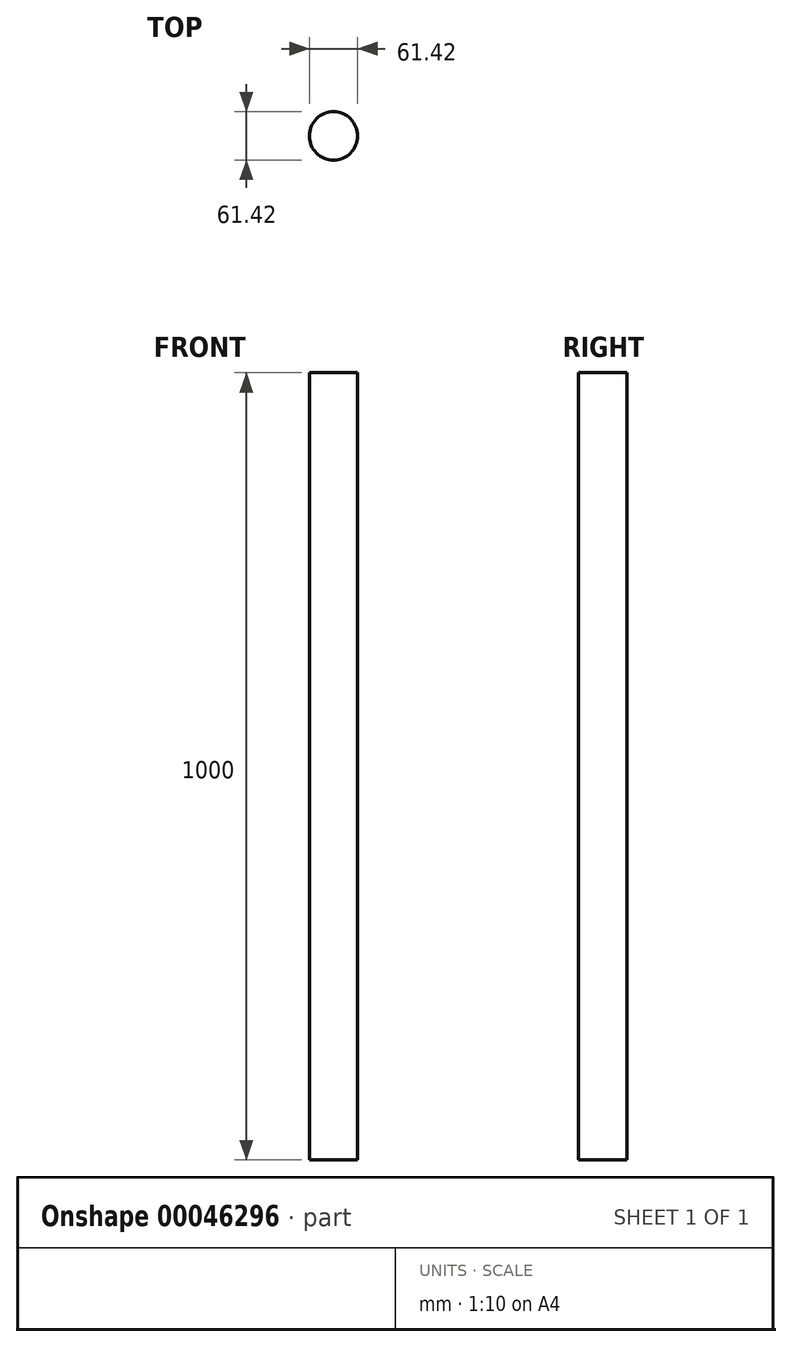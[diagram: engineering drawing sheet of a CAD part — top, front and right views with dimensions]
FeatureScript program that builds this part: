
annotation { "Feature Type Name" : "Feature", "Feature Type Description" : "" }
export const myFeature = defineFeature(function(context is Context, id is Id, definition is map)
    precondition{}
    {
        {
            var Q0;
            Q0=qCreatedBy(makeId("Top.planeOp"),FACE);
            var sketch = newSketch(context, id + "F0", { "sketchPlane" : qUnion([Q0])});
            skCircle(sketch, "E0", {"center": v(0, 0) * mm, "radius": 30.71 * mm});
            skSolve(sketch);
        }
        {
            var Q0;
            Q0=makeQuery(id+"F0.imprint","IMPRINT",FACE,{"disambiguationData":[TD([[makeQuery(id+"F0.imprint","IMPRINT",EDGE,{"derivedFrom":sQuery(id+"F0.wireOp",EDGE,"E0")}),1.0]])]});
            extrude(context, id + "F1", {"entities" : qUnion([Q0]), "depth" : 1000 * mm});
        }
    });
